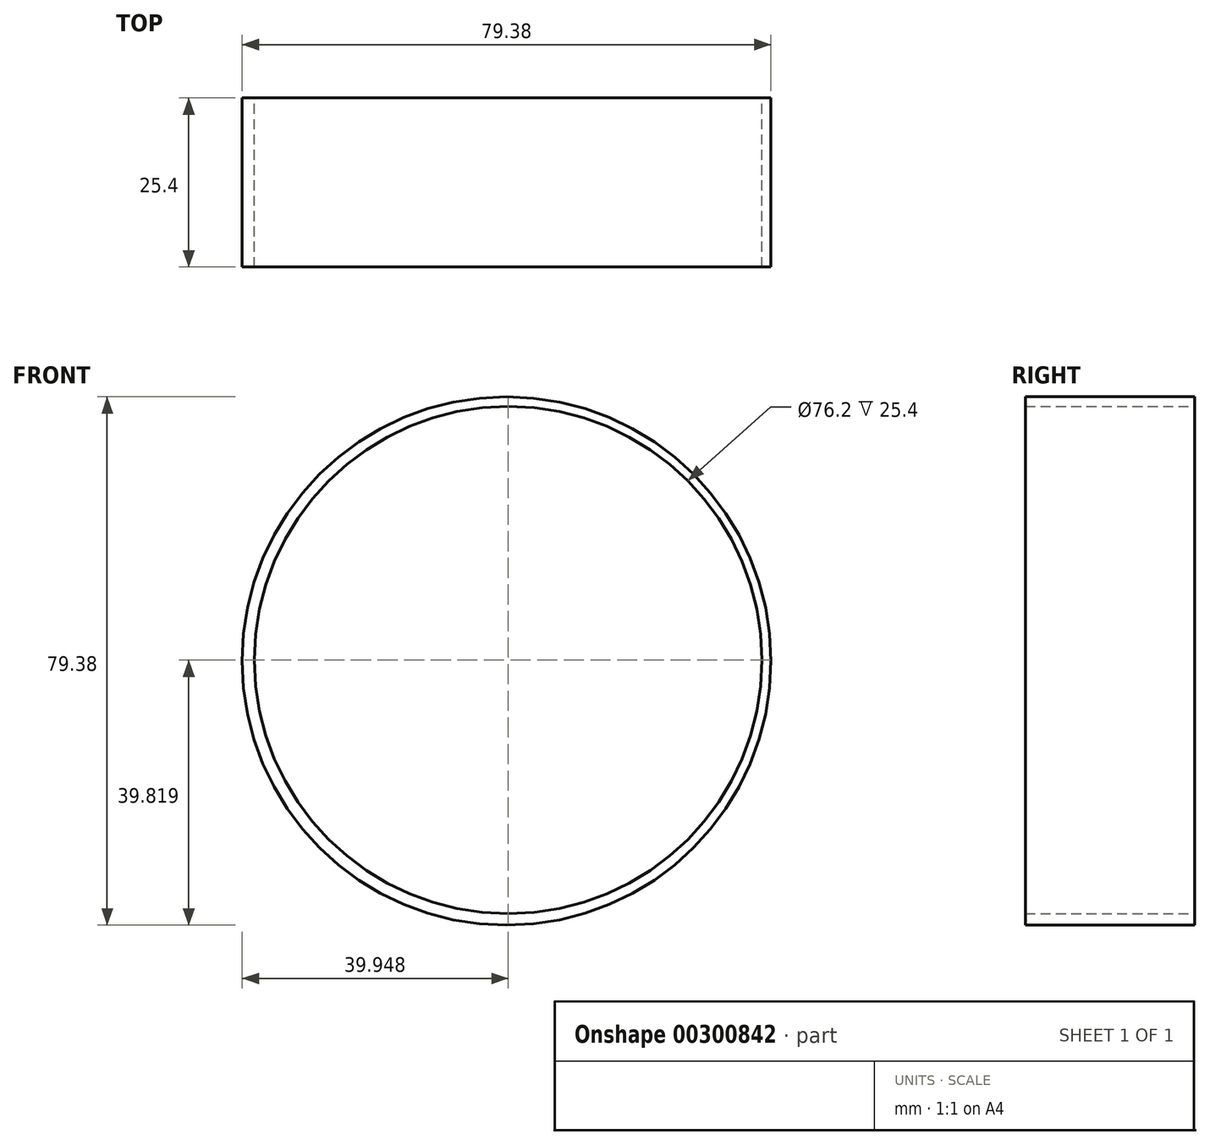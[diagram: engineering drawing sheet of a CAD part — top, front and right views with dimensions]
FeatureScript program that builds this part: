
annotation { "Feature Type Name" : "Feature", "Feature Type Description" : "" }
export const myFeature = defineFeature(function(context is Context, id is Id, definition is map)
    precondition{}
    {
        {
            var Q0;
            Q0=qCreatedBy(makeId("Front.planeOp"),FACE);
            var sketch = newSketch(context, id + "F0", { "sketchPlane" : qUnion([Q0])});
            skCircle(sketch, "E0", {"center": v(0, 0) * mm, "radius": 39.69 * mm});
            skCircle(sketch, "E1", {"center": v(0.26, 0.13) * mm, "radius": 38.1 * mm});
            skSolve(sketch);
        }
        {
            var Q0;
            Q0 = qSketchRegion(id + "F0", true);
            extrude(context, id + "F1", {"entities" : qUnion([Q0]), "depth" : 25.4 * mm});
        }
    });
